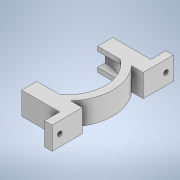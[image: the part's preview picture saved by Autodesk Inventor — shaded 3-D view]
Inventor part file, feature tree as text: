
AUTODESK INVENTOR PART (.ipt)
format: ipt  version: 2022.2 (Build 262287010, 287A)  size: 161,792 bytes
history: native  units: in
note: dims shown in document units (in); Inventor stores cm internally (conversion verified against a paired STEP export)
features: extrude x5, sketch x5, mirror x3, other x1
ambient origin geometry x8: Origin, YZ Plane, XZ Plane, XY Plane, X Axis, Y Axis, Z Axis, Center Point
bodies: Body1 (feature_tree)
feature tree (14):
  other  "Sólido1"
  extrude  "Extrusión1"  Depth=0.1969in
  extrude  "Extrusión2"  Depth=0.5906in TaperAngle=0.0deg
  mirror  "Simetría1"
  extrude  "Extrusión3"  Depth=0.1161in TaperAngle=0.0deg
  mirror  "Simetría2"
  extrude  "Extrusión4"  Depth=0.1969in
  extrude  "Extrusión5"  Depth=0.3937in
  mirror  "Simetría3"
  sketch  "Boceto1"  dims[d0=1.9783in d1=0.1969in]
  sketch  "Boceto2"  dims[d2=0.3937in d3=0.5906in d4=0.0in]
  sketch  "Boceto3"  dims[d5=0.1969in d6=0.1161in d7=0.0in]
  sketch  "Boceto4"  dims[d8=0.1161in d9=0.0in d10=0.1969in]
  sketch  "Boceto5"  dims[d11=0.3937in d12=0.0in d13=0.1181in d14=0.3937in d15=0.0in d17=0.0197in d18=0.0344in d19=0.0197in d20=0.0344in]
